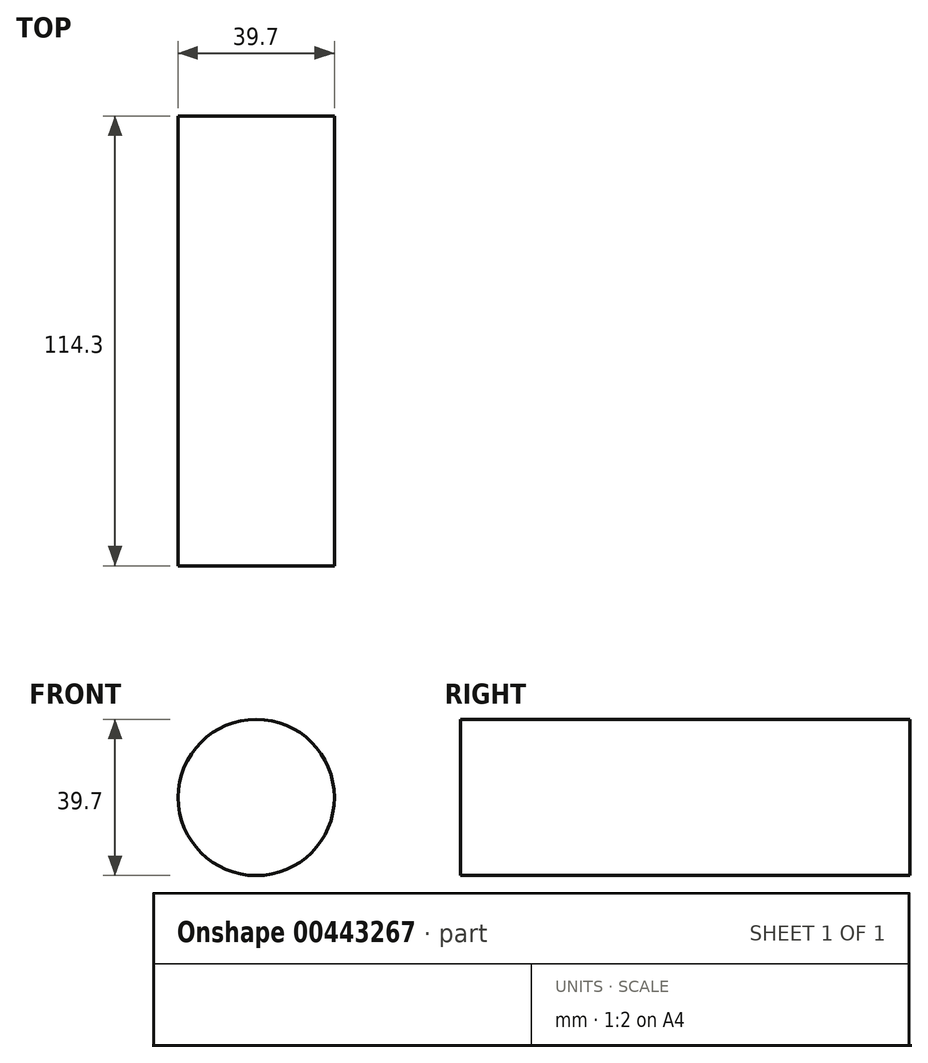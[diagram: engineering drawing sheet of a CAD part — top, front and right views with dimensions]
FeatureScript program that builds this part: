
annotation { "Feature Type Name" : "Feature", "Feature Type Description" : "" }
export const myFeature = defineFeature(function(context is Context, id is Id, definition is map)
    precondition{}
    {
        {
            var Q0;
            Q0=qCreatedBy(makeId("Front.planeOp"),FACE);
            var sketch = newSketch(context, id + "F0", { "sketchPlane" : qUnion([Q0])});
            skCircle(sketch, "E0", {"center": v(0, 0) * mm, "radius": 19.85 * mm});
            skSolve(sketch);
        }
        {
            var Q0;
            Q0 = qSketchRegion(id + "F0", true);
            extrude(context, id + "F1", {"entities" : qUnion([Q0]), "depth" : 114.3 * mm});
        }
    });
